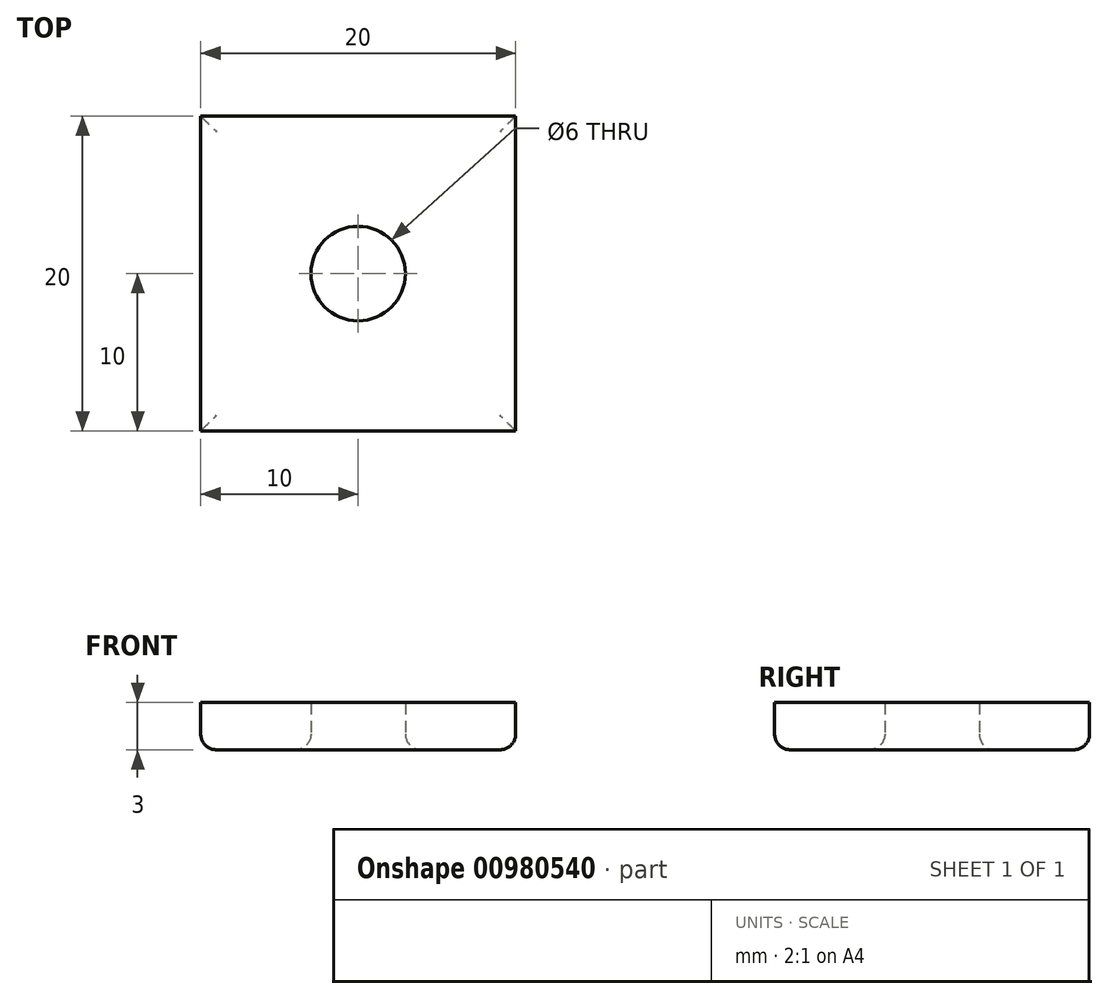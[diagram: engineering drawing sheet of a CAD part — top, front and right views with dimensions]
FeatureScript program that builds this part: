
annotation { "Feature Type Name" : "Feature", "Feature Type Description" : "" }
export const myFeature = defineFeature(function(context is Context, id is Id, definition is map)
    precondition{}
    {
        {
            var Q0;
            Q0=qCreatedBy(makeId("Top.planeOp"),FACE);
            var sketch = newSketch(context, id + "F0", { "sketchPlane" : qUnion([Q0])});
            skLineSegment(sketch, "E0.bottom", {"start": v(0, 0) * mm, "end": v(20, 0) * mm});
            skLineSegment(sketch, "E0.top", {"start": v(0, 20) * mm, "end": v(20, 20) * mm});
            skLineSegment(sketch, "E0.left", {"start": v(0, 0) * mm, "end": v(0, 20) * mm});
            skLineSegment(sketch, "E0.right", {"start": v(20, 0) * mm, "end": v(20, 20) * mm});
            skCircle(sketch, "E1", {"center": v(10, 10) * mm, "radius": 3 * mm});
            skPoint(sketch, "E1.centerSnap0", {"position": v(0, 10) * mm});
            skPoint(sketch, "E1.centerSnap1", {"position": v(10, 0) * mm});
            skSolve(sketch);
        }
        {
            var Q0;
            Q0=makeQuery(id+"F0.imprint","IMPRINT",FACE,{"disambiguationData":[TD([[makeQuery(id+"F0.imprint","IMPRINT",EDGE,{"derivedFrom":sQuery(id+"F0.wireOp",EDGE,"E0.bottom")}),1.0]])]});
            extrude(context, id + "F1", {"entities" : qUnion([Q0]), "depth" : 3 * mm, "offsetDistance" : 25 * mm});
        }
        {
            var Q0;
            Q0=makeQuery(id+"F1.opExtrude","CAP_EDGE",EDGE,{"disambiguationData":[OSD([sQuery(id+"F0.wireOp",EDGE,"E0.left")])],"isStart":true});
            var Q1;
            Q1=makeQuery(id+"F1.opExtrude","CAP_EDGE",EDGE,{"disambiguationData":[OSD([sQuery(id+"F0.wireOp",EDGE,"E0.bottom")])],"isStart":true});
            var Q2;
            Q2=makeQuery(id+"F1.opExtrude","CAP_EDGE",EDGE,{"disambiguationData":[OSD([sQuery(id+"F0.wireOp",EDGE,"E0.right")])],"isStart":true});
            var Q3;
            Q3=makeQuery(id+"F1.opExtrude","CAP_EDGE",EDGE,{"disambiguationData":[OSD([sQuery(id+"F0.wireOp",EDGE,"E0.top")])],"isStart":true});
            var Q4;
            Q4=makeQuery(id+"F1.opExtrude","CAP_EDGE",EDGE,{"disambiguationData":[OSD([sQuery(id+"F0.wireOp",EDGE,"E1")])],"isStart":true});
            fillet(context, id + "F2", {"entities" : qUnion([Q0, Q1, Q2, Q3, Q4]), "radius" : 1 * mm, "tangentPropagation" : true, "allowEdgeOverflow" : false});
        }
    });
